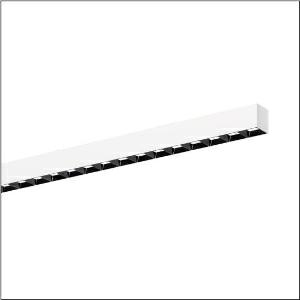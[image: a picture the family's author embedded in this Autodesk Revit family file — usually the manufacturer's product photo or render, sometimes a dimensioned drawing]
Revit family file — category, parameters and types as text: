
# Revit family: silica_r__21_51mx24dc4awb_a921
name_source: partatom
category: Lighting Fixtures
units: mm (PartAtom-declared; Revit-internal decimal feet)

## family parameters
Cut with Voids When Loaded = No
Host = Face
Light Source = No
Part Type = Normal
Room Calculation Point = No
Round Connector Dimension = Use Diameter
Shared = No

## types (1)
- --- (1 x LED, 10800 lm, 73.7 W, 4000K)
    Apparent Load = 74 VA
    CIE Flux Codes = 74 94 99 100 100
    Color Rendering = 80
    Color Temperature = 4000K
    Default Elevation = 1800 mm
    Description = Silica® 21, office luminaire, primary light control with darklight reflector, of PMMA, black, CAT 2 (L<= 3000cd/m²), light emission: direct distribution, primary light characteristic: asymmetric, installation type: surface-mounted, LED, rated luminous flux: 10.800lm, luminous efficacy: 147lm/W, light colour: 840, colour temperature: 4000K, with terminal, 3+2-pole, max. 2.5mm², mains connection: 220..240V, AC, 50/60Hz, rated input power: 73.7W, luminaire housing, of aluminium, traffic white (RAL 9016), length: 3.004mm, width: 53mm, height: 53mm, protection rating (complete): IP20, insulation class (complete): insulation class I (protective earthing), certification: CE, permissible operating ambient temperature: 0..+35°C, standard: EN 50419, packaging unit: 1 piece
    Height = 0 mm  [stored 0 ft]
    Lamp = 1 x LED
    Lamp Light Flux = 10800 lm
    Lamp Power = 73.7 W
    Lamp count = 1
    Length = 3004 mm
    Luminous efficacy = 147 lm/W
    Manufacturer = Siteco
    ModVariant = No
    Model = 51MX24DC4AWB
    Mounting Place = Ceiling
    Mounting Type = Recessed
    Number of Poles = 1
    OnlyDefault = Yes
    Power Factor = 1
    Product Name = Silica® 21
    Product group = office luminaire | ceiling recessed
    ProductGroupID = 401
    Protection Class = Protection class I
    Protection Degree = IP 20
    RLX_Detail_Level = 1
    RLX_Emergency_Light_Flux = 0 lm
    RLX_Emergency_Type = 0
    RLX_Emergency_Type_DB = No
    RlxData = <blob elided: 63105 chars, md5=abd1b387>
    Socket = socket
    Standby Power = 0 W
    System Light Flux = 10800 lm
    System Power = 74 W
    Type Comments = factory setting: luminous flux: 100 % | dim-lin: 254 | 418 mA
    Type Image = l_1297779.jpg
    URL = http://relux.com
    VarID = @adj_053813
    Voltage = 0 V
    Weight = 0.00 kg
    Width = 53 mm

note: [stored X ft] marks values corroborated as IEEE doubles in the binary element streams (Revit-internal decimal feet)

## geometry (parser evidence)
native form markers: Blend x4, Sweep x10
no freeform markers — native parametric forms only
